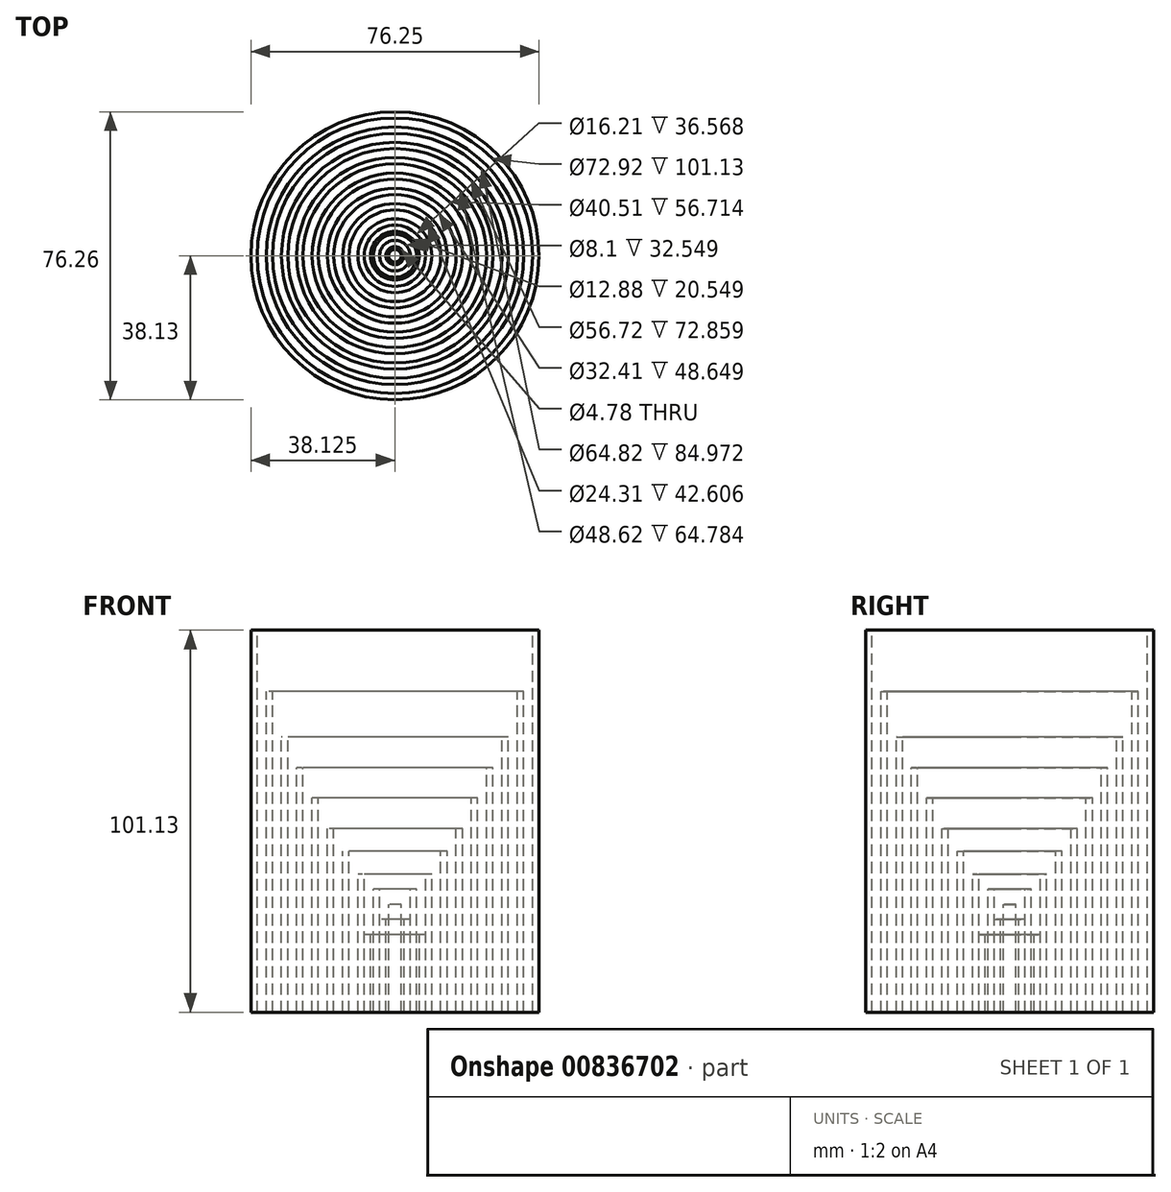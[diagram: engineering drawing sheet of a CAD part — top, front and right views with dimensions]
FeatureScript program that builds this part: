
annotation { "Feature Type Name" : "Feature", "Feature Type Description" : "" }
export const myFeature = defineFeature(function(context is Context, id is Id, definition is map)
    precondition{}
    {
        {
            var Q0;
            Q0=qCreatedBy(makeId("Front.planeOp"),FACE);
            var sketch = newSketch(context, id + "F0", { "sketchPlane" : qUnion([Q0])});
            skLineSegment(sketch, "E0", {"start": v(0, 0) * mm, "end": v(-46.23, 0) * mm});
            skLineSegment(sketch, "E1", {"start": v(-46.23, 0) * mm, "end": v(-46.23, 20.55) * mm});
            skLineSegment(sketch, "E2", {"start": v(-46.23, 20.55) * mm, "end": v(-44.56, 20.55) * mm});
            skLineSegment(sketch, "E3", {"start": v(-44.56, 20.55) * mm, "end": v(-44.56, 0) * mm});
            skLineSegment(sketch, "E4", {"start": v(0, 0) * mm, "end": v(0, 101.13) * mm});
            skLineSegment(sketch, "E5", {"start": v(0, 101.13) * mm, "end": v(-1.66, 101.13) * mm});
            skLineSegment(sketch, "E6", {"start": v(-1.66, 101.13) * mm, "end": v(-1.66, 0) * mm});
            skLineSegment(sketch, "E7", {"start": v(-4.05, 0) * mm, "end": v(-4.05, 84.97) * mm});
            skLineSegment(sketch, "E8", {"start": v(-4.05, 84.97) * mm, "end": v(-5.71, 84.97) * mm});
            skLineSegment(sketch, "E9", {"start": v(-5.71, 84.97) * mm, "end": v(-5.71, 0) * mm});
            skLineSegment(sketch, "E10", {"start": v(-8.1, 0) * mm, "end": v(-8.1, 72.86) * mm});
            skLineSegment(sketch, "E11", {"start": v(-8.1, 72.86) * mm, "end": v(-9.77, 72.86) * mm});
            skLineSegment(sketch, "E12", {"start": v(-9.77, 72.86) * mm, "end": v(-9.77, 0) * mm});
            skLineSegment(sketch, "E13", {"start": v(-12.15, 0) * mm, "end": v(-12.15, 64.78) * mm});
            skLineSegment(sketch, "E14", {"start": v(-12.15, 64.78) * mm, "end": v(-13.82, 64.78) * mm});
            skLineSegment(sketch, "E15", {"start": v(-13.82, 64.78) * mm, "end": v(-13.82, 0) * mm});
            skLineSegment(sketch, "E16", {"start": v(-16.2, 0) * mm, "end": v(-16.2, 56.71) * mm});
            skLineSegment(sketch, "E17", {"start": v(-16.2, 56.71) * mm, "end": v(-17.87, 56.71) * mm});
            skLineSegment(sketch, "E18", {"start": v(-17.87, 56.71) * mm, "end": v(-17.87, 0) * mm});
            skLineSegment(sketch, "E19", {"start": v(-20.26, 0) * mm, "end": v(-20.26, 48.65) * mm});
            skLineSegment(sketch, "E20", {"start": v(-20.26, 48.65) * mm, "end": v(-21.92, 48.65) * mm});
            skLineSegment(sketch, "E21", {"start": v(-21.92, 48.65) * mm, "end": v(-21.92, 0) * mm});
            skLineSegment(sketch, "E22", {"start": v(-24.3, 0) * mm, "end": v(-24.3, 42.6) * mm});
            skLineSegment(sketch, "E23", {"start": v(-24.3, 42.6) * mm, "end": v(-25.97, 42.6) * mm});
            skLineSegment(sketch, "E24", {"start": v(-25.97, 42.6) * mm, "end": v(-25.97, 0) * mm});
            skLineSegment(sketch, "E25", {"start": v(-25.97, 0) * mm, "end": v(-28.36, 0) * mm});
            skLineSegment(sketch, "E26", {"start": v(-28.36, 0) * mm, "end": v(-28.36, 36.57) * mm});
            skLineSegment(sketch, "E27", {"start": v(-28.36, 36.57) * mm, "end": v(-30.02, 36.57) * mm});
            skLineSegment(sketch, "E28", {"start": v(-30.02, 36.57) * mm, "end": v(-30.02, 0) * mm});
            skLineSegment(sketch, "E29", {"start": v(-32.41, 0) * mm, "end": v(-32.41, 32.55) * mm});
            skLineSegment(sketch, "E30", {"start": v(-32.41, 32.55) * mm, "end": v(-34.07, 32.55) * mm});
            skLineSegment(sketch, "E31", {"start": v(-34.07, 32.55) * mm, "end": v(-34.07, 0) * mm});
            skLineSegment(sketch, "E32", {"start": v(-36.46, 0) * mm, "end": v(-36.46, 28.54) * mm});
            skLineSegment(sketch, "E33", {"start": v(-36.46, 28.54) * mm, "end": v(-38.13, 28.54) * mm});
            skLineSegment(sketch, "E34", {"start": v(-38.13, 28.54) * mm, "end": v(-38.13, 0) * mm});
            skLineSegment(sketch, "E35", {"start": v(-40.51, 0) * mm, "end": v(-40.51, 24.54) * mm});
            skLineSegment(sketch, "E36", {"start": v(-40.51, 24.54) * mm, "end": v(-42.18, 24.54) * mm});
            skLineSegment(sketch, "E37", {"start": v(-42.18, 24.54) * mm, "end": v(-42.18, 0) * mm});
            skPoint(sketch, "E38", {"position": v(-46.23, 18.8) * mm});
            skSolve(sketch);
        }
        {
            var Q0;
            Q0 = qSketchRegion(id + "F0", true);
            var Q1;
            Q1=sQuery(id+"F0.wireOp",EDGE,"E34");
            revolve(context, id + "F1", {"surfaceOperationType" : NewSurfaceOperationType.NEW, "entities" : qUnion([Q0]), "axis" : qUnion([Q1]), "revolveType" : RevolveType.FULL});
        }
    });
